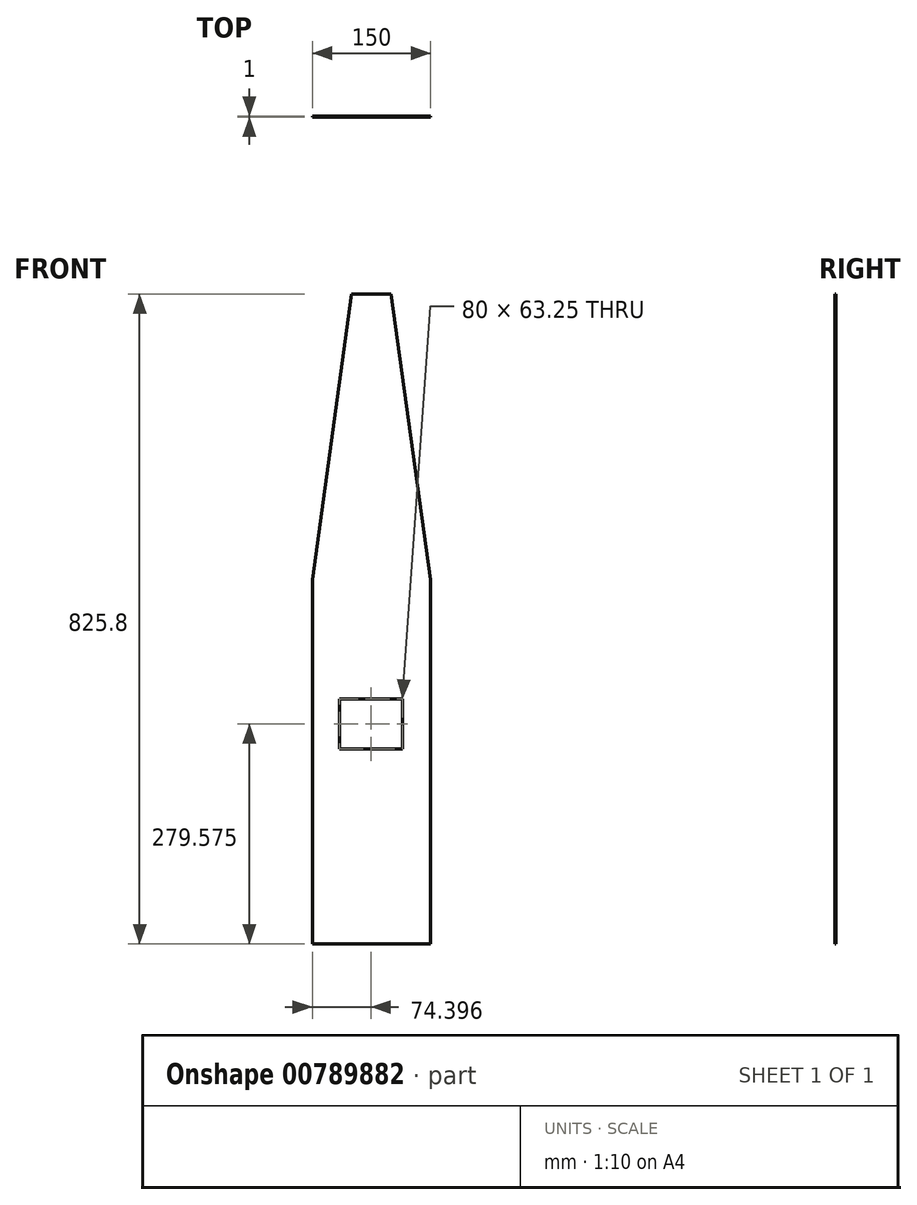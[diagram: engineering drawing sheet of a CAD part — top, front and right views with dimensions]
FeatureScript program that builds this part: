
annotation { "Feature Type Name" : "Feature", "Feature Type Description" : "" }
export const myFeature = defineFeature(function(context is Context, id is Id, definition is map)
    precondition{}
    {
        {
            var Q0;
            Q0=qCreatedBy(makeId("Front.planeOp"),FACE);
            var sketch = newSketch(context, id + "F0", { "sketchPlane" : qUnion([Q0])});
            skLineSegment(sketch, "E0", {"start": v(0, 0) * mm, "end": v(150, 0) * mm});
            skLineSegment(sketch, "E1.0", {"start": v(0, 170) * mm, "end": v(150, 170) * mm});
            skLineSegment(sketch, "E2.0", {"start": v(0, 217.1) * mm, "end": v(150, 217.1) * mm});
            skLineSegment(sketch, "E3.0", {"start": v(0, 227.1) * mm, "end": v(150, 227.1) * mm});
            skLineSegment(sketch, "E4.0", {"start": v(-1.2, 274.2) * mm, "end": v(150, 274.2) * mm});
            skLineSegment(sketch, "E5.0", {"start": v(0, 411.2) * mm, "end": v(150, 411.2) * mm});
            skLineSegment(sketch, "E6", {"start": v(150, 0) * mm, "end": v(150, 463) * mm});
            skLineSegment(sketch, "E7", {"start": v(30, 0) * mm, "end": v(40, 0) * mm});
            skLineSegment(sketch, "E8", {"start": v(120, 0) * mm, "end": v(110, 0) * mm});
            skLineSegment(sketch, "E9", {"start": v(40, 0) * mm, "end": v(40, 170) * mm});
            skLineSegment(sketch, "E10", {"start": v(30, 0) * mm, "end": v(30, 170) * mm});
            skLineSegment(sketch, "E11", {"start": v(110, 0) * mm, "end": v(110, 170) * mm});
            skLineSegment(sketch, "E12", {"start": v(120, 0) * mm, "end": v(120, 170) * mm});
            skLineSegment(sketch, "E13", {"start": v(150, 657) * mm, "end": v(24.5, 657) * mm});
            skLineSegment(sketch, "E14", {"start": v(150, 708.8) * mm, "end": v(0, 708.8) * mm});
            skLineSegment(sketch, "E15", {"start": v(75, 825.8) * mm, "end": v(100, 825.8) * mm});
            skLineSegment(sketch, "E16", {"start": v(100, 825.8) * mm, "end": v(50, 825.8) * mm});
            skLineSegment(sketch, "E17", {"start": v(100, 825.8) * mm, "end": v(150, 463) * mm});
            skLineSegment(sketch, "E18", {"start": v(0, 0) * mm, "end": v(0, 411.2) * mm});
            skLineSegment(sketch, "E19", {"start": v(0, 411.2) * mm, "end": v(0, 463) * mm});
            skLineSegment(sketch, "E20", {"start": v(0, 463) * mm, "end": v(50, 825.8) * mm});
            skLineSegment(sketch, "E21", {"start": v(0, 463) * mm, "end": v(150, 463) * mm});
            skLineSegment(sketch, "E22", {"start": v(114.4, 274.2) * mm, "end": v(34.4, 274.2) * mm});
            skLineSegment(sketch, "E23", {"start": v(34.4, 274.2) * mm, "end": v(34.4, 311.2) * mm});
            skLineSegment(sketch, "E24", {"start": v(34.4, 311.2) * mm, "end": v(114.4, 311.2) * mm});
            skLineSegment(sketch, "E25", {"start": v(114.4, 311.2) * mm, "end": v(114.4, 274.2) * mm});
            skLineSegment(sketch, "E26", {"start": v(34.4, 274.2) * mm, "end": v(34.4, 247.95) * mm});
            skLineSegment(sketch, "E27", {"start": v(34.4, 247.95) * mm, "end": v(114.4, 247.95) * mm});
            skLineSegment(sketch, "E28", {"start": v(114.4, 247.95) * mm, "end": v(114.4, 274.2) * mm});
            skSolve(sketch);
        }
        {
            var Q0;
            Q0=qSketchRegion(id+"F0",true);
            extrude(context, id + "F1", {"entities" : qUnion([Q0]), "depth" : 1 * mm, "offsetDistance" : 25 * mm});
        }
    });
